# Revit family: AF5300A 67-73-79-85-90 C
name_source: partatom
category: HLS-Bauteile
revit_build: Autodesk Revit 2017 (Build: 20160720_1515(x64)
units: mm (PartAtom-declared; Revit-internal decimal feet)

## family parameters
Arbeitsebenenbasiert = Nein
Beim Laden mit Abzugskörper schneiden = Nein
Bemaßung runder Anschluss = Durchmesser verwenden
Gemeinsam genutzt = Nein
Immer vertikal = Ja
OmniClass-Nummer = 23.75.00.00
OmniClass-Titel = Climate Control (HVAC)
Raumberechnungspunkt = Nein
Teiletyp = Normal

## types (5) — shared parameters
Beschreibung = High efficiency air cooled
Casing color = White
Compressor = 2
Condensation = Air
Depth = 850 mm  [stored 2.78871 ft]
Gas = R410A
Height = 1830 mm  [stored 6.00394 ft]
Hersteller = Bosch
Installation = Outdoor installation
Machine material = Galvanized Steel
Power supply = 380-415V 3N~50Hz/60Hz
Series = VRF
Width = 1730 mm  [stored 5.67585 ft]
clearance access behind = 1000 mm  [stored 3.28084 ft]
clearance access front = 1000 mm  [stored 3.28084 ft]
clearance access left = 1000 mm  [stored 3.28084 ft]
clearance access right = 1000 mm  [stored 3.28084 ft]

## per-type parameters (varying)
| type | Air Flow max | Cooling Capacity | Cooling Power Input | Gas pipe | Heating Capacity | Heating Power Input | Liquid pipe | Maximum Fuse Amps | Minimum Circuit Amps | Net Weight |
| AF5300A 67 C-3 | 25000.000 m³/h | 67.000 kW | 18.100 kW | 31.8 mm  [stored 0.104331 ft] | 67.000 kW | 14.900 kW | 19.1 mm  [stored 0.062664 ft] | 70 A | 48 A | 430.00 kg |
| AF5300A 73 C-3 | 25000.000 m³/h | 73.000 kW | 20.900 kW | 31.8 mm  [stored 0.104331 ft] | 73.000 kW | 17.600 kW | 22.2 mm  [stored 0.0728346 ft] | 70 A | 53 A | 430.00 kg |
| AF5300A 79 C-3 | 25000.000 m³/h | 78.500 kW | 24.200 kW | 31.8 mm  [stored 0.104331 ft] | 78.500 kW | 20.700 kW | 22.2 mm  [stored 0.0728346 ft] | 70 A | 59 A | 430.00 kg |
| AF5300A 85 C-3 | 24000.000 m³/h | 85.000 kW | 27.400 kW | 38.1 mm  [stored 0.125 ft] | 85.000 kW | 23.000 kW | 22.2 mm  [stored 0.0728346 ft] | 80 A | 65 A | 475.00 kg |
| AF5300A 90 C-3 | 24000.000 m³/h | 90.000 kW | 31.000 kW | 38.1 mm  [stored 0.125 ft] | 90.000 kW | 25.700 kW | 22.2 mm  [stored 0.0728346 ft] | 80 A | 67 A | 475.00 kg |

note: column(s) folded — value = type name in every type: Modell

note: [stored X ft] marks values corroborated as IEEE doubles in the binary element streams (Revit-internal decimal feet)

## geometry (parser evidence)
native form markers: Sweep x6
no freeform markers — native parametric forms only
